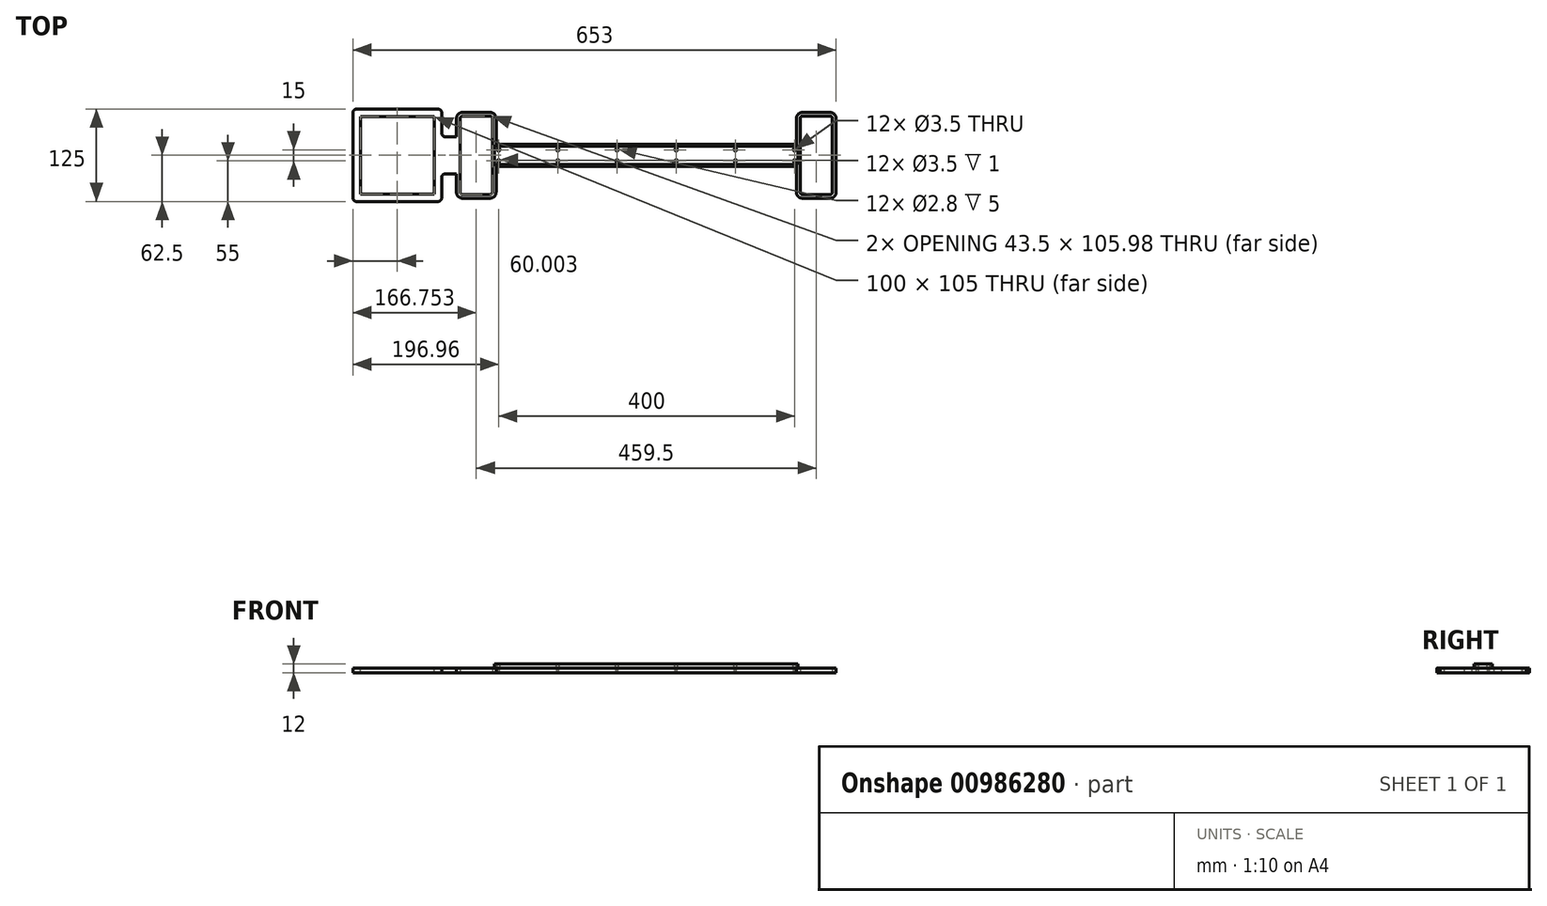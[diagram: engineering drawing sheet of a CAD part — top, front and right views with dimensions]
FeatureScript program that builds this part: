
annotation { "Feature Type Name" : "Feature", "Feature Type Description" : "" }
export const myFeature = defineFeature(function(context is Context, id is Id, definition is map)
    precondition{}
    {
        {
            var Q0;
            Q0=qCreatedBy(makeId("Top.planeOp"),FACE);
            var sketch = newSketch(context, id + "F0", { "sketchPlane" : qUnion([Q0])});
            skLineSegment(sketch, "E0.0", {"start": v(-21.69, 50) * mm, "end": v(-21.69, -50) * mm});
            skLineSegment(sketch, "E1.0", {"start": v(-18.69, 53) * mm, "end": v(18.81, 53) * mm});
            skPoint(sketch, "E2.0", {"position": v(-20.8, 52.11) * mm});
            skPoint(sketch, "E3.0", {"position": v(20.93, 52.11) * mm});
            skLineSegment(sketch, "E4.0", {"start": v(21.81, 50) * mm, "end": v(21.81, -50) * mm});
            skCircle(sketch, "E5.0", {"center": v(12.31, 33) * mm, "radius": 1.75 * mm});
            skCircle(sketch, "E6.0", {"center": v(-12.69, 33) * mm, "radius": 1.75 * mm});
            skArc(sketch, "E7.0", {"start": v(-18.69, 53) * mm, "mid": v(-20.8, 52.11) * mm, "end": v(-21.69, 50) * mm});
            skArc(sketch, "E8.0", {"start": v(21.81, 50) * mm, "mid": v(20.93, 52.11) * mm, "end": v(18.81, 53) * mm});
            skCircle(sketch, "E9.0", {"center": v(12.31, -33) * mm, "radius": 1.75 * mm});
            skCircle(sketch, "E10.0", {"center": v(-12.69, -33) * mm, "radius": 1.75 * mm});
            skPoint(sketch, "E11.0", {"position": v(-20.8, -52.11) * mm});
            skArc(sketch, "E12.0", {"start": v(-21.69, -50) * mm, "mid": v(-20.8, -52.11) * mm, "end": v(-18.69, -53) * mm});
            skLineSegment(sketch, "E13.0", {"start": v(18.81, -53) * mm, "end": v(-18.69, -53) * mm});
            skPoint(sketch, "E14.0", {"position": v(20.93, -52.11) * mm});
            skArc(sketch, "E15.0", {"start": v(18.81, -53) * mm, "mid": v(20.93, -52.11) * mm, "end": v(21.81, -50) * mm});
            skSolve(sketch);
        }
        {
            var Q0;
            Q0=makeQuery(id+"F0.imprint","IMPRINT",FACE,{"disambiguationData":[TD([[makeQuery(id+"F0.imprint","IMPRINT",EDGE,{"derivedFrom":sQuery(id+"F0.wireOp",EDGE,"E0.0")}),1.0]])]});
            extrude(context, id + "F1", {"entities" : qUnion([Q0]), "depth" : 3 * mm, "offsetDistance" : 25 * mm});
        }
        {
            var Q0;
            Q0=qCreatedBy(makeId("Top.planeOp"),FACE);
            var sketch = newSketch(context, id + "F2", { "sketchPlane" : qUnion([Q0])});
            skArc(sketch, "E16.0", {"start": v(-18.69, 58) * mm, "mid": v(-24.34, 55.65) * mm, "end": v(-26.69, 50) * mm});
            skLineSegment(sketch, "E16.1", {"start": v(-18.69, 58) * mm, "end": v(18.81, 58) * mm});
            skLineSegment(sketch, "E16.2", {"start": v(-26.69, 50) * mm, "end": v(-26.69, 30) * mm});
            skArc(sketch, "E16.3", {"start": v(26.81, 50) * mm, "mid": v(24.47, 55.65) * mm, "end": v(18.81, 58) * mm});
            skArc(sketch, "E16.4", {"start": v(-26.69, -50) * mm, "mid": v(-24.34, -55.65) * mm, "end": v(-18.69, -58) * mm});
            skLineSegment(sketch, "E16.5", {"start": v(18.81, -58) * mm, "end": v(-18.69, -58) * mm});
            skArc(sketch, "E16.6", {"start": v(18.81, -58) * mm, "mid": v(24.47, -55.65) * mm, "end": v(26.81, -50) * mm});
            skLineSegment(sketch, "E16.7", {"start": v(26.81, 50) * mm, "end": v(26.81, -50) * mm});
            skLineSegment(sketch, "E17", {"start": v(-21.69, 0) * mm, "end": v(-227.69, 0) * mm});
            skLineSegment(sketch, "E18.0", {"start": v(-26.69, -30) * mm, "end": v(-229.69, -30) * mm});
            skLineSegment(sketch, "E19.0", {"start": v(-26.69, 30) * mm, "end": v(-229.69, 30) * mm});
            skLineSegment(sketch, "E20", {"start": v(-229.69, 30) * mm, "end": v(-229.69, -30) * mm});
            skLineSegment(sketch, "E21.trimOffspring", {"start": v(-26.69, -30) * mm, "end": v(-26.69, -50) * mm});
            skLineSegment(sketch, "E22.0", {"start": v(-21.69, 50) * mm, "end": v(-21.69, -50) * mm});
            skLineSegment(sketch, "E23.0", {"start": v(-18.69, 53) * mm, "end": v(18.81, 53) * mm});
            skLineSegment(sketch, "E24.0", {"start": v(21.81, 50) * mm, "end": v(21.81, -50) * mm});
            skLineSegment(sketch, "E25.0", {"start": v(18.81, -53) * mm, "end": v(-18.69, -53) * mm});
            skArc(sketch, "E26.0", {"start": v(-21.69, -50) * mm, "mid": v(-20.8, -52.11) * mm, "end": v(-18.69, -53) * mm});
            skArc(sketch, "E27.0", {"start": v(18.81, -53) * mm, "mid": v(20.93, -52.11) * mm, "end": v(21.81, -50) * mm});
            skArc(sketch, "E28.0", {"start": v(21.81, 50) * mm, "mid": v(20.93, 52.11) * mm, "end": v(18.81, 53) * mm});
            skArc(sketch, "E29.0", {"start": v(-18.69, 53) * mm, "mid": v(-20.8, 52.11) * mm, "end": v(-21.69, 50) * mm});
            skSolve(sketch);
        }
        {
            var Q0;
            Q0=makeQuery(id+"F2.imprint","IMPRINT",FACE,{"disambiguationData":[TD([[makeQuery(id+"F2.imprint","IMPRINT",EDGE,{"derivedFrom":sQuery(id+"F2.wireOp",EDGE,"E16.0")}),1.0]])]});
            extrude(context, id + "F3", {"entities" : qUnion([Q0]), "operationType" : NewBodyOperationType.ADD, "depth" : 6 * mm, "offsetDistance" : 25 * mm});
        }
        {
            var Q0;
            Q0=makeQuery(id+"F3.opExtrude","SWEPT_FACE",FACE,{"disambiguationData":[OSD([sQuery(id+"F2.wireOp",EDGE,"E20")])]});
            cPlane(context, id + "F4", {"entities" : qUnion([Q0]), "cplaneType" : CPlaneType.OFFSET, "offset" : 0 * mm, "width" : 150 * mm, "height" : 150 * mm});
        }
        {
            var Q0;
            Q0=makeQuery(id+"F1.opExtrude","SWEPT_BODY",BODY,{"disambiguationData":[OSD([sQuery(id+"F0.wireOp",EDGE,"E0.0"),sQuery(id+"F0.wireOp",EDGE,"E1.0"),sQuery(id+"F0.wireOp",EDGE,"E4.0"),sQuery(id+"F0.wireOp",EDGE,"E5.0"),sQuery(id+"F0.wireOp",EDGE,"E6.0"),sQuery(id+"F0.wireOp",EDGE,"E7.0"),sQuery(id+"F0.wireOp",EDGE,"E8.0"),sQuery(id+"F0.wireOp",EDGE,"E9.0"),sQuery(id+"F0.wireOp",EDGE,"E10.0"),sQuery(id+"F0.wireOp",EDGE,"E12.0"),sQuery(id+"F0.wireOp",EDGE,"E13.0"),sQuery(id+"F0.wireOp",EDGE,"E15.0")])]});
            var Q1;
            Q1=qCreatedBy(id+"F4.planeOp",FACE);
            mirror(context, id + "F5", {"operationType" : NewBodyOperationType.ADD, "entities" : qUnion([Q0]), "mirrorPlane" : qUnion([Q1])});
        }
        {
            var Q0;
            {var subQ0=makeQuery(id+"F3.opExtrude","CAP_FACE",FACE,{"disambiguationData":[OSD([sQuery(id+"F2.wireOp",EDGE,"E16.0"),sQuery(id+"F2.wireOp",EDGE,"E16.1"),sQuery(id+"F2.wireOp",EDGE,"E16.2"),sQuery(id+"F2.wireOp",EDGE,"E16.3"),sQuery(id+"F2.wireOp",EDGE,"E16.4"),sQuery(id+"F2.wireOp",EDGE,"E16.5"),sQuery(id+"F2.wireOp",EDGE,"E16.6"),sQuery(id+"F2.wireOp",EDGE,"E16.7"),sQuery(id+"F2.wireOp",EDGE,"E18.0"),sQuery(id+"F2.wireOp",EDGE,"E19.0"),sQuery(id+"F2.wireOp",EDGE,"E20"),sQuery(id+"F2.wireOp",EDGE,"E21.trimOffspring"),sQuery(id+"F2.wireOp",EDGE,"E22.0"),sQuery(id+"F2.wireOp",EDGE,"E23.0"),sQuery(id+"F2.wireOp",EDGE,"E24.0"),sQuery(id+"F2.wireOp",EDGE,"E25.0"),sQuery(id+"F2.wireOp",EDGE,"E26.0"),sQuery(id+"F2.wireOp",EDGE,"E27.0"),sQuery(id+"F2.wireOp",EDGE,"E28.0"),sQuery(id+"F2.wireOp",EDGE,"E29.0")])],"isStart":false});Q0=makeQuery(id+"F5.boolean.opBoolean","MERGE",FACE,{"derivedFrom":[subQ0,makeQuery(id+"F5.opPattern","COPY",FACE,{"derivedFrom":subQ0,"instanceName":"1"})]});}
            var sketch = newSketch(context, id + "F6", { "sketchPlane" : qUnion([Q0])});
            skLineSegment(sketch, "E30", {"start": v(-229.69, 30) * mm, "end": v(-169.69, 30) * mm});
            skLineSegment(sketch, "E31", {"start": v(-169.69, 30) * mm, "end": v(-169.69, 58) * mm});
            skLineSegment(sketch, "E32", {"start": v(-169.69, 58) * mm, "end": v(-289.69, 58) * mm});
            skLineSegment(sketch, "E33", {"start": v(-289.69, 58) * mm, "end": v(-289.69, 30) * mm});
            skLineSegment(sketch, "E34", {"start": v(-289.69, 30) * mm, "end": v(-229.69, 30) * mm});
            skSolve(sketch);
        }
        {
            var Q0;
            Q0=makeQuery(id+"F6.imprint","IMPRINT",FACE,{"disambiguationData":[TD([[makeQuery(id+"F6.imprint","IMPRINT",EDGE,{"derivedFrom":sQuery(id+"F6.wireOp",EDGE,"E30")}),-1.0]])]});
            var Q1;
            {var subQ0=makeQuery(id+"F3.boolean.opBoolean","MERGE",FACE,{"derivedFrom":[makeQuery(id+"F1.opExtrude","CAP_FACE",FACE,{"disambiguationData":[OSD([sQuery(id+"F0.wireOp",EDGE,"E0.0"),sQuery(id+"F0.wireOp",EDGE,"E1.0"),sQuery(id+"F0.wireOp",EDGE,"E4.0"),sQuery(id+"F0.wireOp",EDGE,"E5.0"),sQuery(id+"F0.wireOp",EDGE,"E6.0"),sQuery(id+"F0.wireOp",EDGE,"E7.0"),sQuery(id+"F0.wireOp",EDGE,"E8.0"),sQuery(id+"F0.wireOp",EDGE,"E9.0"),sQuery(id+"F0.wireOp",EDGE,"E10.0"),sQuery(id+"F0.wireOp",EDGE,"E12.0"),sQuery(id+"F0.wireOp",EDGE,"E13.0"),sQuery(id+"F0.wireOp",EDGE,"E15.0")])],"isStart":true}),makeQuery(id+"F3.opExtrude","CAP_FACE",FACE,{"disambiguationData":[OSD([sQuery(id+"F2.wireOp",EDGE,"E16.0"),sQuery(id+"F2.wireOp",EDGE,"E16.1"),sQuery(id+"F2.wireOp",EDGE,"E16.2"),sQuery(id+"F2.wireOp",EDGE,"E16.3"),sQuery(id+"F2.wireOp",EDGE,"E16.4"),sQuery(id+"F2.wireOp",EDGE,"E16.5"),sQuery(id+"F2.wireOp",EDGE,"E16.6"),sQuery(id+"F2.wireOp",EDGE,"E16.7"),sQuery(id+"F2.wireOp",EDGE,"E18.0"),sQuery(id+"F2.wireOp",EDGE,"E19.0"),sQuery(id+"F2.wireOp",EDGE,"E20"),sQuery(id+"F2.wireOp",EDGE,"E21.trimOffspring"),sQuery(id+"F2.wireOp",EDGE,"E22.0"),sQuery(id+"F2.wireOp",EDGE,"E23.0"),sQuery(id+"F2.wireOp",EDGE,"E24.0"),sQuery(id+"F2.wireOp",EDGE,"E25.0"),sQuery(id+"F2.wireOp",EDGE,"E26.0"),sQuery(id+"F2.wireOp",EDGE,"E27.0"),sQuery(id+"F2.wireOp",EDGE,"E28.0"),sQuery(id+"F2.wireOp",EDGE,"E29.0")])],"isStart":true})]});Q1=makeQuery(id+"F5.boolean.opBoolean","MERGE",FACE,{"derivedFrom":[subQ0,makeQuery(id+"F5.opPattern","COPY",FACE,{"derivedFrom":subQ0,"instanceName":"1"})]});}
            extrude(context, id + "F7", {"entities" : qUnion([Q0]), "operationType" : NewBodyOperationType.ADD, "endBound" : BoundingType.UP_TO_SURFACE, "oppositeDirection" : true, "depth" : 25 * mm, "endBoundEntityFace" : qUnion([Q1]), "offsetDistance" : 25 * mm});
        }
        {
            var Q0;
            Q0=makeQuery(id+"F7.opExtrude","SWEPT_EDGE",EDGE,{"disambiguationData":[OSD([sQuery(id+"F6.wireOp",EDGE,"E31"),sQuery(id+"F6.wireOp",EDGE,"E32")])]});
            var Q1;
            Q1=makeQuery(id+"F7.opExtrude","SWEPT_EDGE",EDGE,{"disambiguationData":[OSD([sQuery(id+"F2.wireOp",EDGE,"E19.0"),sQuery(id+"F6.wireOp",EDGE,"E30"),sQuery(id+"F6.wireOp",EDGE,"E31")])]});
            var Q2;
            Q2=makeQuery(id+"F7.opExtrude","SWEPT_EDGE",EDGE,{"disambiguationData":[OSD([sQuery(id+"F6.wireOp",EDGE,"E32"),sQuery(id+"F6.wireOp",EDGE,"E33")])]});
            var Q3;
            Q3=makeQuery(id+"F7.opExtrude","SWEPT_EDGE",EDGE,{"disambiguationData":[OSD([sQuery(id+"F2.wireOp",EDGE,"E19.0"),sQuery(id+"F6.wireOp",EDGE,"E33"),sQuery(id+"F6.wireOp",EDGE,"E34")])]});
            fillet(context, id + "F8", {"entities" : qUnion([Q0, Q1, Q2, Q3]), "radius" : 10 * mm, "tangentPropagation" : true, "allowEdgeOverflow" : false});
        }
        {
            var Q0;
            {var subQ0=makeQuery(id+"F3.opExtrude","CAP_FACE",FACE,{"disambiguationData":[OSD([sQuery(id+"F2.wireOp",EDGE,"E16.0"),sQuery(id+"F2.wireOp",EDGE,"E16.1"),sQuery(id+"F2.wireOp",EDGE,"E16.2"),sQuery(id+"F2.wireOp",EDGE,"E16.3"),sQuery(id+"F2.wireOp",EDGE,"E16.4"),sQuery(id+"F2.wireOp",EDGE,"E16.5"),sQuery(id+"F2.wireOp",EDGE,"E16.6"),sQuery(id+"F2.wireOp",EDGE,"E16.7"),sQuery(id+"F2.wireOp",EDGE,"E18.0"),sQuery(id+"F2.wireOp",EDGE,"E19.0"),sQuery(id+"F2.wireOp",EDGE,"E20"),sQuery(id+"F2.wireOp",EDGE,"E21.trimOffspring"),sQuery(id+"F2.wireOp",EDGE,"E22.0"),sQuery(id+"F2.wireOp",EDGE,"E23.0"),sQuery(id+"F2.wireOp",EDGE,"E24.0"),sQuery(id+"F2.wireOp",EDGE,"E25.0"),sQuery(id+"F2.wireOp",EDGE,"E26.0"),sQuery(id+"F2.wireOp",EDGE,"E27.0"),sQuery(id+"F2.wireOp",EDGE,"E28.0"),sQuery(id+"F2.wireOp",EDGE,"E29.0")])],"isStart":false});Q0=makeQuery(id+"F7.boolean.opBoolean","MERGE",FACE,{"derivedFrom":[makeQuery(id+"F5.boolean.opBoolean","MERGE",FACE,{"derivedFrom":[subQ0,makeQuery(id+"F5.opPattern","COPY",FACE,{"derivedFrom":subQ0,"instanceName":"1"})]}),makeQuery(id+"F7.opExtrude","CAP_FACE",FACE,{"disambiguationData":[OSD([sQuery(id+"F6.wireOp",EDGE,"E30"),sQuery(id+"F6.wireOp",EDGE,"E31"),sQuery(id+"F6.wireOp",EDGE,"E32"),sQuery(id+"F6.wireOp",EDGE,"E33"),sQuery(id+"F6.wireOp",EDGE,"E34")])],"isStart":true})]});}
            var sketch = newSketch(context, id + "F9", { "sketchPlane" : qUnion([Q0])});
            skLineSegment(sketch, "E35", {"start": v(-437.69, 0) * mm, "end": v(-13.9, 0) * mm, "construction": true});
            skLineSegment(sketch, "E36.bottom", {"start": v(-274.69, 23) * mm, "end": v(-184.69, 23) * mm});
            skLineSegment(sketch, "E36.top", {"start": v(-274.69, 48) * mm, "end": v(-184.69, 48) * mm});
            skLineSegment(sketch, "E36.left", {"start": v(-279.69, 28) * mm, "end": v(-279.69, 43) * mm});
            skLineSegment(sketch, "E36.right", {"start": v(-179.69, 28) * mm, "end": v(-179.69, 43) * mm});
            skPoint(sketch, "E36.middle", {"position": v(-229.69, 35.5) * mm});
            skPoint(sketch, "E37.visualSharp", {"position": v(-279.69, 48) * mm});
            skArc(sketch, "E37.filletArc", {"start": v(-274.69, 48) * mm, "mid": v(-278.22, 46.53) * mm, "end": v(-279.69, 43) * mm});
            skPoint(sketch, "E38.visualSharp", {"position": v(-179.69, 48) * mm});
            skArc(sketch, "E38.filletArc", {"start": v(-179.69, 43) * mm, "mid": v(-181.15, 46.53) * mm, "end": v(-184.69, 48) * mm});
            skPoint(sketch, "E39.visualSharp", {"position": v(-179.69, 23) * mm});
            skArc(sketch, "E39.filletArc", {"start": v(-184.69, 23) * mm, "mid": v(-181.15, 24.45) * mm, "end": v(-179.69, 28) * mm});
            skPoint(sketch, "E40.visualSharp", {"position": v(-279.69, 23) * mm});
            skArc(sketch, "E40.filletArc", {"start": v(-279.69, 28) * mm, "mid": v(-278.22, 24.45) * mm, "end": v(-274.69, 23) * mm});
            skSolve(sketch);
        }
        {
            var Q0;
            Q0=makeQuery(id+"F9.imprint","IMPRINT",FACE,{"disambiguationData":[TD([[makeQuery(id+"F9.imprint","IMPRINT",EDGE,{"derivedFrom":sQuery(id+"F9.wireOp",EDGE,"E36.bottom")}),1.0]])]});
            extrude(context, id + "F10", {"entities" : qUnion([Q0]), "operationType" : NewBodyOperationType.REMOVE, "oppositeDirection" : true, "depth" : 25 * mm, "offsetDistance" : 25 * mm});
        }
        {
            var Q0;
            Q0=makeQuery(id+"F5.opPattern","COPY",EDGE,{"derivedFrom":makeQuery(id+"F3.opExtrude","SWEPT_EDGE",EDGE,{"disambiguationData":[OSD([sQuery(id+"F2.wireOp",EDGE,"E16.2"),sQuery(id+"F2.wireOp",EDGE,"E19.0")])]}),"instanceName":"1"});
            var Q1;
            Q1=makeQuery(id+"F5.opPattern","COPY",EDGE,{"derivedFrom":makeQuery(id+"F3.opExtrude","SWEPT_EDGE",EDGE,{"disambiguationData":[OSD([sQuery(id+"F2.wireOp",EDGE,"E18.0"),sQuery(id+"F2.wireOp",EDGE,"E21.trimOffspring")])]}),"instanceName":"1"});
            var Q2;
            Q2=makeQuery(id+"F3.opExtrude","SWEPT_EDGE",EDGE,{"disambiguationData":[OSD([sQuery(id+"F2.wireOp",EDGE,"E18.0"),sQuery(id+"F2.wireOp",EDGE,"E21.trimOffspring")])]});
            var Q3;
            Q3=makeQuery(id+"F3.opExtrude","SWEPT_EDGE",EDGE,{"disambiguationData":[OSD([sQuery(id+"F2.wireOp",EDGE,"E16.2"),sQuery(id+"F2.wireOp",EDGE,"E19.0")])]});
            fillet(context, id + "F11", {"entities" : qUnion([Q0, Q1, Q2, Q3]), "radius" : 5 * mm, "tangentPropagation" : true, "allowEdgeOverflow" : false});
        }
        {
            var Q0;
            {var subQ0=makeQuery(id+"F3.opExtrude","CAP_FACE",FACE,{"disambiguationData":[OSD([sQuery(id+"F2.wireOp",EDGE,"E16.0"),sQuery(id+"F2.wireOp",EDGE,"E16.1"),sQuery(id+"F2.wireOp",EDGE,"E16.2"),sQuery(id+"F2.wireOp",EDGE,"E16.3"),sQuery(id+"F2.wireOp",EDGE,"E16.4"),sQuery(id+"F2.wireOp",EDGE,"E16.5"),sQuery(id+"F2.wireOp",EDGE,"E16.6"),sQuery(id+"F2.wireOp",EDGE,"E16.7"),sQuery(id+"F2.wireOp",EDGE,"E18.0"),sQuery(id+"F2.wireOp",EDGE,"E19.0"),sQuery(id+"F2.wireOp",EDGE,"E20"),sQuery(id+"F2.wireOp",EDGE,"E21.trimOffspring"),sQuery(id+"F2.wireOp",EDGE,"E22.0"),sQuery(id+"F2.wireOp",EDGE,"E23.0"),sQuery(id+"F2.wireOp",EDGE,"E24.0"),sQuery(id+"F2.wireOp",EDGE,"E25.0"),sQuery(id+"F2.wireOp",EDGE,"E26.0"),sQuery(id+"F2.wireOp",EDGE,"E27.0"),sQuery(id+"F2.wireOp",EDGE,"E28.0"),sQuery(id+"F2.wireOp",EDGE,"E29.0")])],"isStart":false});Q0=makeQuery(id+"F7.boolean.opBoolean","MERGE",FACE,{"derivedFrom":[makeQuery(id+"F5.boolean.opBoolean","MERGE",FACE,{"derivedFrom":[subQ0,makeQuery(id+"F5.opPattern","COPY",FACE,{"derivedFrom":subQ0,"instanceName":"1"})]}),makeQuery(id+"F7.opExtrude","CAP_FACE",FACE,{"disambiguationData":[OSD([sQuery(id+"F6.wireOp",EDGE,"E30"),sQuery(id+"F6.wireOp",EDGE,"E31"),sQuery(id+"F6.wireOp",EDGE,"E32"),sQuery(id+"F6.wireOp",EDGE,"E33"),sQuery(id+"F6.wireOp",EDGE,"E34")])],"isStart":true})]});}
            var sketch = newSketch(context, id + "F12", { "sketchPlane" : qUnion([Q0])});
            skLineSegment(sketch, "E41", {"start": v(-229.69, 0) * mm, "end": v(-229.69, 17.75) * mm, "construction": true});
            skPoint(sketch, "E41.startSnap0", {"position": v(-229.69, -30) * mm});
            skLineSegment(sketch, "E42.bottom", {"start": v(-434.69, -12.5) * mm, "end": v(-24.69, -12.5) * mm});
            skLineSegment(sketch, "E42.top", {"start": v(-434.69, 12.5) * mm, "end": v(-24.69, 12.5) * mm});
            skLineSegment(sketch, "E42.left", {"start": v(-434.69, -12.5) * mm, "end": v(-434.69, 12.5) * mm});
            skLineSegment(sketch, "E42.right", {"start": v(-24.69, -12.5) * mm, "end": v(-24.69, 12.5) * mm});
            skPoint(sketch, "E42.middle", {"position": v(-229.69, 0) * mm});
            skSolve(sketch);
        }
        {
            var Q0;
            Q0=makeQuery(id+"F12.imprint","IMPRINT",FACE,{"disambiguationData":[TD([[makeQuery(id+"F12.imprint","IMPRINT",EDGE,{"derivedFrom":sQuery(id+"F12.wireOp",EDGE,"E42.bottom")}),1.0]])]});
            extrude(context, id + "F13", {"entities" : qUnion([Q0]), "depth" : 6 * mm, "offsetDistance" : 25 * mm});
        }
        {
            var Q0;
            Q0=makeQuery(id+"F13.opExtrude","CAP_FACE",FACE,{"disambiguationData":[OSD([sQuery(id+"F12.wireOp",EDGE,"E42.bottom"),sQuery(id+"F12.wireOp",EDGE,"E42.top"),sQuery(id+"F12.wireOp",EDGE,"E42.left"),sQuery(id+"F12.wireOp",EDGE,"E42.right")])],"isStart":false});
            var sketch = newSketch(context, id + "F14", { "sketchPlane" : qUnion([Q0])});
            skLineSegment(sketch, "E43.bottom", {"start": v(-429.23, -7.5) * mm, "end": v(-29.23, -7.5) * mm, "construction": true});
            skLineSegment(sketch, "E43.top", {"start": v(-429.23, 7.5) * mm, "end": v(-29.23, 7.5) * mm, "construction": true});
            skLineSegment(sketch, "E43.left", {"start": v(-429.23, -7.5) * mm, "end": v(-429.23, 7.5) * mm, "construction": true});
            skLineSegment(sketch, "E43.right", {"start": v(-29.23, -7.5) * mm, "end": v(-29.23, 7.5) * mm, "construction": true});
            skPoint(sketch, "E43.middle", {"position": v(-229.23, 0) * mm});
            skCircle(sketch, "E44", {"center": v(-429.23, 7.5) * mm, "radius": 1.75 * mm});
            skCircle(sketch, "E45", {"center": v(-429.23, -7.5) * mm, "radius": 1.75 * mm});
            skCircle(sketch, "E46.1.0.0", {"center": v(-349.23, 7.5) * mm, "radius": 1.75 * mm});
            skCircle(sketch, "E46.2.0.0", {"center": v(-269.23, 7.5) * mm, "radius": 1.75 * mm});
            skCircle(sketch, "E46.3.0.0", {"center": v(-189.23, 7.5) * mm, "radius": 1.75 * mm});
            skCircle(sketch, "E46.4.0.0", {"center": v(-109.23, 7.5) * mm, "radius": 1.75 * mm});
            skLineSegment(sketch, "E46.direction1", {"start": v(-429.23, 7.5) * mm, "end": v(-349.23, 7.5) * mm, "construction": true});
            skCircle(sketch, "E47.1.0.0", {"center": v(-349.23, -7.5) * mm, "radius": 1.75 * mm});
            skCircle(sketch, "E47.2.0.0", {"center": v(-269.23, -7.5) * mm, "radius": 1.75 * mm});
            skCircle(sketch, "E47.3.0.0", {"center": v(-189.23, -7.5) * mm, "radius": 1.75 * mm});
            skCircle(sketch, "E47.4.0.0", {"center": v(-109.23, -7.5) * mm, "radius": 1.75 * mm});
            skLineSegment(sketch, "E47.direction1", {"start": v(-429.23, -7.5) * mm, "end": v(-349.23, -7.5) * mm, "construction": true});
            skCircle(sketch, "E48.0.5.0", {"center": v(-29.23, -7.5) * mm, "radius": 1.75 * mm});
            skCircle(sketch, "E49.0.5.0", {"center": v(-29.23, 7.5) * mm, "radius": 1.75 * mm});
            skSolve(sketch);
        }
        {
            var Q0;
            Q0=makeQuery(id+"F14.imprint","IMPRINT",FACE,{"disambiguationData":[TD([[makeQuery(id+"F14.imprint","IMPRINT",EDGE,{"derivedFrom":sQuery(id+"F14.wireOp",EDGE,"E44")}),1.0]])]});
            var Q1;
            Q1=makeQuery(id+"F14.imprint","IMPRINT",FACE,{"disambiguationData":[TD([[makeQuery(id+"F14.imprint","IMPRINT",EDGE,{"derivedFrom":sQuery(id+"F14.wireOp",EDGE,"E45")}),1.0]])]});
            var Q2;
            Q2=makeQuery(id+"F14.imprint","IMPRINT",FACE,{"disambiguationData":[TD([[makeQuery(id+"F14.imprint","IMPRINT",EDGE,{"derivedFrom":sQuery(id+"F14.wireOp",EDGE,"E47.1.0.0")}),1.0]])]});
            var Q3;
            Q3=makeQuery(id+"F14.imprint","IMPRINT",FACE,{"disambiguationData":[TD([[makeQuery(id+"F14.imprint","IMPRINT",EDGE,{"derivedFrom":sQuery(id+"F14.wireOp",EDGE,"E46.1.0.0")}),1.0]])]});
            var Q4;
            Q4=makeQuery(id+"F14.imprint","IMPRINT",FACE,{"disambiguationData":[TD([[makeQuery(id+"F14.imprint","IMPRINT",EDGE,{"derivedFrom":sQuery(id+"F14.wireOp",EDGE,"E46.2.0.0")}),1.0]])]});
            var Q5;
            Q5=makeQuery(id+"F14.imprint","IMPRINT",FACE,{"disambiguationData":[TD([[makeQuery(id+"F14.imprint","IMPRINT",EDGE,{"derivedFrom":sQuery(id+"F14.wireOp",EDGE,"E47.2.0.0")}),1.0]])]});
            var Q6;
            Q6=makeQuery(id+"F14.imprint","IMPRINT",FACE,{"disambiguationData":[TD([[makeQuery(id+"F14.imprint","IMPRINT",EDGE,{"derivedFrom":sQuery(id+"F14.wireOp",EDGE,"E47.3.0.0")}),1.0]])]});
            var Q7;
            Q7=makeQuery(id+"F14.imprint","IMPRINT",FACE,{"disambiguationData":[TD([[makeQuery(id+"F14.imprint","IMPRINT",EDGE,{"derivedFrom":sQuery(id+"F14.wireOp",EDGE,"E46.3.0.0")}),1.0]])]});
            var Q8;
            Q8=makeQuery(id+"F14.imprint","IMPRINT",FACE,{"disambiguationData":[TD([[makeQuery(id+"F14.imprint","IMPRINT",EDGE,{"derivedFrom":sQuery(id+"F14.wireOp",EDGE,"E47.4.0.0")}),1.0]])]});
            var Q9;
            Q9=makeQuery(id+"F14.imprint","IMPRINT",FACE,{"disambiguationData":[TD([[makeQuery(id+"F14.imprint","IMPRINT",EDGE,{"derivedFrom":sQuery(id+"F14.wireOp",EDGE,"E46.4.0.0")}),1.0]])]});
            var Q10;
            Q10=makeQuery(id+"F14.imprint","IMPRINT",FACE,{"disambiguationData":[TD([[makeQuery(id+"F14.imprint","IMPRINT",EDGE,{"derivedFrom":sQuery(id+"F14.wireOp",EDGE,"E48.0.5.0")}),1.0]])]});
            var Q11;
            Q11=makeQuery(id+"F14.imprint","IMPRINT",FACE,{"disambiguationData":[TD([[makeQuery(id+"F14.imprint","IMPRINT",EDGE,{"derivedFrom":sQuery(id+"F14.wireOp",EDGE,"E49.0.5.0")}),1.0]])]});
            extrude(context, id + "F15", {"entities" : qUnion([Q0, Q1, Q2, Q3, Q4, Q5, Q6, Q7, Q8, Q9, Q10, Q11]), "operationType" : NewBodyOperationType.REMOVE, "oppositeDirection" : true, "depth" : 7 * mm, "offsetDistance" : 25 * mm});
        }
        {
            var Q0;
            {var subQ0=makeQuery(id+"F3.opExtrude","CAP_FACE",FACE,{"disambiguationData":[OSD([sQuery(id+"F2.wireOp",EDGE,"E16.0"),sQuery(id+"F2.wireOp",EDGE,"E16.1"),sQuery(id+"F2.wireOp",EDGE,"E16.2"),sQuery(id+"F2.wireOp",EDGE,"E16.3"),sQuery(id+"F2.wireOp",EDGE,"E16.4"),sQuery(id+"F2.wireOp",EDGE,"E16.5"),sQuery(id+"F2.wireOp",EDGE,"E16.6"),sQuery(id+"F2.wireOp",EDGE,"E16.7"),sQuery(id+"F2.wireOp",EDGE,"E18.0"),sQuery(id+"F2.wireOp",EDGE,"E19.0"),sQuery(id+"F2.wireOp",EDGE,"E20"),sQuery(id+"F2.wireOp",EDGE,"E21.trimOffspring"),sQuery(id+"F2.wireOp",EDGE,"E22.0"),sQuery(id+"F2.wireOp",EDGE,"E23.0"),sQuery(id+"F2.wireOp",EDGE,"E24.0"),sQuery(id+"F2.wireOp",EDGE,"E25.0"),sQuery(id+"F2.wireOp",EDGE,"E26.0"),sQuery(id+"F2.wireOp",EDGE,"E27.0"),sQuery(id+"F2.wireOp",EDGE,"E28.0"),sQuery(id+"F2.wireOp",EDGE,"E29.0")])],"isStart":false});Q0=makeQuery(id+"F7.boolean.opBoolean","MERGE",FACE,{"derivedFrom":[makeQuery(id+"F5.boolean.opBoolean","MERGE",FACE,{"derivedFrom":[subQ0,makeQuery(id+"F5.opPattern","COPY",FACE,{"derivedFrom":subQ0,"instanceName":"1"})]}),makeQuery(id+"F7.opExtrude","CAP_FACE",FACE,{"disambiguationData":[OSD([sQuery(id+"F6.wireOp",EDGE,"E30"),sQuery(id+"F6.wireOp",EDGE,"E31"),sQuery(id+"F6.wireOp",EDGE,"E32"),sQuery(id+"F6.wireOp",EDGE,"E33"),sQuery(id+"F6.wireOp",EDGE,"E34")])],"isStart":true})]});}
            var sketch = newSketch(context, id + "F16", { "sketchPlane" : qUnion([Q0])});
            skCircle(sketch, "E50", {"center": v(-429.23, 7.5) * mm, "radius": 1.4 * mm});
            skCircle(sketch, "E51.1.0.0", {"center": v(-349.23, 7.5) * mm, "radius": 1.4 * mm});
            skCircle(sketch, "E51.2.0.0", {"center": v(-269.23, 7.5) * mm, "radius": 1.4 * mm});
            skLineSegment(sketch, "E51.direction1", {"start": v(-429.23, 7.5) * mm, "end": v(-349.23, 7.5) * mm, "construction": true});
            skCircle(sketch, "E52.0.3.0", {"center": v(-189.23, 7.5) * mm, "radius": 1.4 * mm});
            skCircle(sketch, "E52.0.4.0", {"center": v(-109.23, 7.5) * mm, "radius": 1.4 * mm});
            skCircle(sketch, "E52.0.5.0", {"center": v(-29.23, 7.5) * mm, "radius": 1.4 * mm});
            skCircle(sketch, "E53", {"center": v(-429.23, -7.5) * mm, "radius": 1.4 * mm});
            skCircle(sketch, "E54.1.0.0", {"center": v(-349.23, -7.5) * mm, "radius": 1.4 * mm});
            skCircle(sketch, "E54.2.0.0", {"center": v(-269.23, -7.5) * mm, "radius": 1.4 * mm});
            skLineSegment(sketch, "E54.direction1", {"start": v(-429.23, -7.5) * mm, "end": v(-349.23, -7.5) * mm, "construction": true});
            skCircle(sketch, "E55.0.3.0", {"center": v(-189.23, -7.5) * mm, "radius": 1.4 * mm});
            skCircle(sketch, "E55.0.4.0", {"center": v(-109.23, -7.5) * mm, "radius": 1.4 * mm});
            skCircle(sketch, "E55.0.5.0", {"center": v(-29.23, -7.5) * mm, "radius": 1.4 * mm});
            skSolve(sketch);
        }
        {
            var Q0;
            Q0 = qSketchRegion(id + "F16", true);
            extrude(context, id + "F17", {"entities" : qUnion([Q0]), "operationType" : NewBodyOperationType.REMOVE, "oppositeDirection" : true, "depth" : 25 * mm, "offsetDistance" : 25 * mm});
        }
        {
            var Q0;
            Q0=makeQuery(id+"F5.opPattern","COPY",FACE,{"derivedFrom":makeQuery(id+"F1.opExtrude","CAP_FACE",FACE,{"disambiguationData":[OSD([sQuery(id+"F0.wireOp",EDGE,"E0.0"),sQuery(id+"F0.wireOp",EDGE,"E1.0"),sQuery(id+"F0.wireOp",EDGE,"E4.0"),sQuery(id+"F0.wireOp",EDGE,"E5.0"),sQuery(id+"F0.wireOp",EDGE,"E6.0"),sQuery(id+"F0.wireOp",EDGE,"E7.0"),sQuery(id+"F0.wireOp",EDGE,"E8.0"),sQuery(id+"F0.wireOp",EDGE,"E9.0"),sQuery(id+"F0.wireOp",EDGE,"E10.0"),sQuery(id+"F0.wireOp",EDGE,"E12.0"),sQuery(id+"F0.wireOp",EDGE,"E13.0"),sQuery(id+"F0.wireOp",EDGE,"E15.0")])],"isStart":false}),"instanceName":"1"});
            extrude(context, id + "F18", {"entities" : qUnion([Q0]), "operationType" : NewBodyOperationType.REMOVE, "oppositeDirection" : true, "depth" : 25 * mm, "offsetDistance" : 25 * mm});
        }
        {
            var Q0;
            Q0=makeQuery(id+"F1.opExtrude","CAP_FACE",FACE,{"disambiguationData":[OSD([sQuery(id+"F0.wireOp",EDGE,"E0.0"),sQuery(id+"F0.wireOp",EDGE,"E1.0"),sQuery(id+"F0.wireOp",EDGE,"E4.0"),sQuery(id+"F0.wireOp",EDGE,"E5.0"),sQuery(id+"F0.wireOp",EDGE,"E6.0"),sQuery(id+"F0.wireOp",EDGE,"E7.0"),sQuery(id+"F0.wireOp",EDGE,"E8.0"),sQuery(id+"F0.wireOp",EDGE,"E9.0"),sQuery(id+"F0.wireOp",EDGE,"E10.0"),sQuery(id+"F0.wireOp",EDGE,"E12.0"),sQuery(id+"F0.wireOp",EDGE,"E13.0"),sQuery(id+"F0.wireOp",EDGE,"E15.0")])],"isStart":false});
            extrude(context, id + "F19", {"entities" : qUnion([Q0]), "operationType" : NewBodyOperationType.REMOVE, "oppositeDirection" : true, "depth" : 25 * mm, "offsetDistance" : 25 * mm});
        }
        {
            var Q0;
            {var subQ0=makeQuery(id+"F3.opExtrude","CAP_FACE",FACE,{"disambiguationData":[OSD([sQuery(id+"F2.wireOp",EDGE,"E16.0"),sQuery(id+"F2.wireOp",EDGE,"E16.1"),sQuery(id+"F2.wireOp",EDGE,"E16.2"),sQuery(id+"F2.wireOp",EDGE,"E16.3"),sQuery(id+"F2.wireOp",EDGE,"E16.4"),sQuery(id+"F2.wireOp",EDGE,"E16.5"),sQuery(id+"F2.wireOp",EDGE,"E16.6"),sQuery(id+"F2.wireOp",EDGE,"E16.7"),sQuery(id+"F2.wireOp",EDGE,"E18.0"),sQuery(id+"F2.wireOp",EDGE,"E19.0"),sQuery(id+"F2.wireOp",EDGE,"E20"),sQuery(id+"F2.wireOp",EDGE,"E21.trimOffspring"),sQuery(id+"F2.wireOp",EDGE,"E22.0"),sQuery(id+"F2.wireOp",EDGE,"E23.0"),sQuery(id+"F2.wireOp",EDGE,"E24.0"),sQuery(id+"F2.wireOp",EDGE,"E25.0"),sQuery(id+"F2.wireOp",EDGE,"E26.0"),sQuery(id+"F2.wireOp",EDGE,"E27.0"),sQuery(id+"F2.wireOp",EDGE,"E28.0"),sQuery(id+"F2.wireOp",EDGE,"E29.0")])],"isStart":false});Q0=makeQuery(id+"F7.boolean.opBoolean","MERGE",FACE,{"derivedFrom":[makeQuery(id+"F5.boolean.opBoolean","MERGE",FACE,{"derivedFrom":[subQ0,makeQuery(id+"F5.opPattern","COPY",FACE,{"derivedFrom":subQ0,"instanceName":"1"})]}),makeQuery(id+"F7.opExtrude","CAP_FACE",FACE,{"disambiguationData":[OSD([sQuery(id+"F6.wireOp",EDGE,"E30"),sQuery(id+"F6.wireOp",EDGE,"E31"),sQuery(id+"F6.wireOp",EDGE,"E32"),sQuery(id+"F6.wireOp",EDGE,"E33"),sQuery(id+"F6.wireOp",EDGE,"E34")])],"isStart":true})]});}
            var sketch = newSketch(context, id + "F20", { "sketchPlane" : qUnion([Q0])});
            skLineSegment(sketch, "E56", {"start": v(-432.69, 35) * mm, "end": v(-432.69, -35) * mm});
            skLineSegment(sketch, "E57", {"start": v(-26.69, 35) * mm, "end": v(-26.69, -35) * mm});
            skLineSegment(sketch, "E58", {"start": v(-432.69, 0) * mm, "end": v(-26.69, 0) * mm});
            skLineSegment(sketch, "E59.0", {"start": v(-432.69, -15) * mm, "end": v(-26.69, -15) * mm});
            skLineSegment(sketch, "E60.0", {"start": v(-432.69, 15) * mm, "end": v(-26.69, 15) * mm});
            skLineSegment(sketch, "E61", {"start": v(-432.69, 35) * mm, "end": v(-303.71, 72.78) * mm});
            skLineSegment(sketch, "E62", {"start": v(-303.71, 72.78) * mm, "end": v(-151.14, 72.78) * mm});
            skLineSegment(sketch, "E63", {"start": v(-151.14, 72.78) * mm, "end": v(-26.69, 35) * mm});
            skLineSegment(sketch, "E64", {"start": v(-432.69, -35) * mm, "end": v(-388.9, -53.91) * mm});
            skLineSegment(sketch, "E65", {"start": v(-388.9, -53.91) * mm, "end": v(-192.66, -53.91) * mm});
            skLineSegment(sketch, "E66", {"start": v(-192.66, -53.91) * mm, "end": v(-26.69, -35) * mm});
            skSolve(sketch);
        }
        {
            var Q0;
            {var subQ16=sQuery(id+"F20.wireOp",EDGE,"E60.0");Q0=makeQuery(id+"F20.imprint","IMPRINT",FACE,{"disambiguationData":[TD([[makeQuery(id+"F20.imprint","IMPRINT",EDGE,{"derivedFrom":subQ16}),1.0]])]});}
            var Q1;
            Q1=makeQuery(id+"F20.imprint","IMPRINT",FACE,{"disambiguationData":[TD([[makeQuery(id+"F20.imprint","IMPRINT",EDGE,{"derivedFrom":sQuery(id+"F20.wireOp",EDGE,"E61")}),-1.0]])]});
            var Q2;
            {var subQ0=sQuery(id+"F20.wireOp",EDGE,"E59.0");Q2=makeQuery(id+"F20.imprint","IMPRINT",FACE,{"disambiguationData":[TD([[makeQuery(id+"F20.imprint","IMPRINT",EDGE,{"derivedFrom":subQ0}),-1.0]])]});}
            var Q3;
            Q3=makeQuery(id+"F20.imprint","IMPRINT",FACE,{"disambiguationData":[TD([[makeQuery(id+"F20.imprint","IMPRINT",EDGE,{"derivedFrom":sQuery(id+"F20.wireOp",EDGE,"E64")}),1.0]])]});
            extrude(context, id + "F21", {"entities" : qUnion([Q0, Q1, Q2, Q3]), "operationType" : NewBodyOperationType.REMOVE, "oppositeDirection" : true, "depth" : 25 * mm, "offsetDistance" : 25 * mm});
        }
        {
            var Q0;
            {var subQ0=makeQuery(id+"F3.opExtrude","CAP_FACE",FACE,{"disambiguationData":[OSD([sQuery(id+"F2.wireOp",EDGE,"E16.0"),sQuery(id+"F2.wireOp",EDGE,"E16.1"),sQuery(id+"F2.wireOp",EDGE,"E16.2"),sQuery(id+"F2.wireOp",EDGE,"E16.3"),sQuery(id+"F2.wireOp",EDGE,"E16.4"),sQuery(id+"F2.wireOp",EDGE,"E16.5"),sQuery(id+"F2.wireOp",EDGE,"E16.6"),sQuery(id+"F2.wireOp",EDGE,"E16.7"),sQuery(id+"F2.wireOp",EDGE,"E18.0"),sQuery(id+"F2.wireOp",EDGE,"E19.0"),sQuery(id+"F2.wireOp",EDGE,"E20"),sQuery(id+"F2.wireOp",EDGE,"E21.trimOffspring"),sQuery(id+"F2.wireOp",EDGE,"E22.0"),sQuery(id+"F2.wireOp",EDGE,"E23.0"),sQuery(id+"F2.wireOp",EDGE,"E24.0"),sQuery(id+"F2.wireOp",EDGE,"E25.0"),sQuery(id+"F2.wireOp",EDGE,"E26.0"),sQuery(id+"F2.wireOp",EDGE,"E27.0"),sQuery(id+"F2.wireOp",EDGE,"E28.0"),sQuery(id+"F2.wireOp",EDGE,"E29.0")])],"isStart":false});Q0=makeQuery(id+"F7.boolean.opBoolean","MERGE",FACE,{"derivedFrom":[makeQuery(id+"F5.boolean.opBoolean","MERGE",FACE,{"derivedFrom":[subQ0,makeQuery(id+"F5.opPattern","COPY",FACE,{"derivedFrom":subQ0,"instanceName":"1"})]}),makeQuery(id+"F7.opExtrude","CAP_FACE",FACE,{"disambiguationData":[OSD([sQuery(id+"F6.wireOp",EDGE,"E30"),sQuery(id+"F6.wireOp",EDGE,"E31"),sQuery(id+"F6.wireOp",EDGE,"E32"),sQuery(id+"F6.wireOp",EDGE,"E33"),sQuery(id+"F6.wireOp",EDGE,"E34")])],"isStart":true})]});}
            var sketch = newSketch(context, id + "F22", { "sketchPlane" : qUnion([Q0])});
            skLineSegment(sketch, "E67", {"start": v(-486.19, 0) * mm, "end": v(-566.19, 0) * mm, "construction": true});
            skLineSegment(sketch, "E68.bottom", {"start": v(-616.19, -52.5) * mm, "end": v(-516.19, -52.5) * mm});
            skLineSegment(sketch, "E68.top", {"start": v(-616.19, 52.5) * mm, "end": v(-516.19, 52.5) * mm});
            skLineSegment(sketch, "E68.left", {"start": v(-616.19, -52.5) * mm, "end": v(-616.19, 52.5) * mm});
            skLineSegment(sketch, "E68.right", {"start": v(-516.19, -52.5) * mm, "end": v(-516.19, 52.5) * mm});
            skPoint(sketch, "E68.middle", {"position": v(-566.19, 0) * mm});
            skLineSegment(sketch, "E69.0", {"start": v(-626.19, 62.5) * mm, "end": v(-506.19, 62.5) * mm});
            skLineSegment(sketch, "E69.1", {"start": v(-626.19, -62.5) * mm, "end": v(-626.19, 62.5) * mm});
            skLineSegment(sketch, "E69.2", {"start": v(-626.19, -62.5) * mm, "end": v(-506.19, -62.5) * mm});
            skLineSegment(sketch, "E69.3", {"start": v(-506.19, -62.5) * mm, "end": v(-506.19, 62.5) * mm});
            skLineSegment(sketch, "E70", {"start": v(-486.19, 25) * mm, "end": v(-506.19, 25) * mm});
            skLineSegment(sketch, "E71.MirrorCS", {"start": v(-486.19, -25) * mm, "end": v(-506.19, -25) * mm});
            skSolve(sketch);
        }
        {
            var Q0;
            {var subQ0=sQuery(id+"F22.wireOp",EDGE,"E70");Q0=makeQuery(id+"F22.imprint","IMPRINT",FACE,{"disambiguationData":[TD([[makeQuery(id+"F22.imprint","IMPRINT",EDGE,{"derivedFrom":subQ0}),1.0]])]});}
            var Q1;
            Q1=makeQuery(id+"F22.imprint","IMPRINT",FACE,{"disambiguationData":[TD([[makeQuery(id+"F22.imprint","IMPRINT",EDGE,{"derivedFrom":sQuery(id+"F22.wireOp",EDGE,"E68.bottom")}),-1.0]])]});
            var Q2;
            {var subQ0=makeQuery(id+"F3.boolean.opBoolean","MERGE",FACE,{"derivedFrom":[makeQuery(id+"F1.opExtrude","CAP_FACE",FACE,{"disambiguationData":[OSD([sQuery(id+"F0.wireOp",EDGE,"E0.0"),sQuery(id+"F0.wireOp",EDGE,"E1.0"),sQuery(id+"F0.wireOp",EDGE,"E4.0"),sQuery(id+"F0.wireOp",EDGE,"E5.0"),sQuery(id+"F0.wireOp",EDGE,"E6.0"),sQuery(id+"F0.wireOp",EDGE,"E7.0"),sQuery(id+"F0.wireOp",EDGE,"E8.0"),sQuery(id+"F0.wireOp",EDGE,"E9.0"),sQuery(id+"F0.wireOp",EDGE,"E10.0"),sQuery(id+"F0.wireOp",EDGE,"E12.0"),sQuery(id+"F0.wireOp",EDGE,"E13.0"),sQuery(id+"F0.wireOp",EDGE,"E15.0")])],"isStart":true}),makeQuery(id+"F3.opExtrude","CAP_FACE",FACE,{"disambiguationData":[OSD([sQuery(id+"F2.wireOp",EDGE,"E16.0"),sQuery(id+"F2.wireOp",EDGE,"E16.1"),sQuery(id+"F2.wireOp",EDGE,"E16.2"),sQuery(id+"F2.wireOp",EDGE,"E16.3"),sQuery(id+"F2.wireOp",EDGE,"E16.4"),sQuery(id+"F2.wireOp",EDGE,"E16.5"),sQuery(id+"F2.wireOp",EDGE,"E16.6"),sQuery(id+"F2.wireOp",EDGE,"E16.7"),sQuery(id+"F2.wireOp",EDGE,"E18.0"),sQuery(id+"F2.wireOp",EDGE,"E19.0"),sQuery(id+"F2.wireOp",EDGE,"E20"),sQuery(id+"F2.wireOp",EDGE,"E21.trimOffspring"),sQuery(id+"F2.wireOp",EDGE,"E22.0"),sQuery(id+"F2.wireOp",EDGE,"E23.0"),sQuery(id+"F2.wireOp",EDGE,"E24.0"),sQuery(id+"F2.wireOp",EDGE,"E25.0"),sQuery(id+"F2.wireOp",EDGE,"E26.0"),sQuery(id+"F2.wireOp",EDGE,"E27.0"),sQuery(id+"F2.wireOp",EDGE,"E28.0"),sQuery(id+"F2.wireOp",EDGE,"E29.0")])],"isStart":true})]});Q2=makeQuery(id+"F7.boolean.opBoolean","MERGE",FACE,{"derivedFrom":[makeQuery(id+"F5.boolean.opBoolean","MERGE",FACE,{"derivedFrom":[subQ0,makeQuery(id+"F5.opPattern","COPY",FACE,{"derivedFrom":subQ0,"instanceName":"1"})]}),makeQuery(id+"F7.opExtrude","CAP_FACE",FACE,{"disambiguationData":[OSD([sQuery(id+"F6.wireOp",EDGE,"E30"),sQuery(id+"F6.wireOp",EDGE,"E31"),sQuery(id+"F6.wireOp",EDGE,"E32"),sQuery(id+"F6.wireOp",EDGE,"E33"),sQuery(id+"F6.wireOp",EDGE,"E34")])],"isStart":false})]});}
            extrude(context, id + "F23", {"entities" : qUnion([Q0, Q1]), "operationType" : NewBodyOperationType.ADD, "endBound" : BoundingType.UP_TO_SURFACE, "oppositeDirection" : true, "depth" : 25 * mm, "endBoundEntityFace" : qUnion([Q2]), "offsetDistance" : 25 * mm});
        }
        {
            var Q0;
            Q0=makeQuery(id+"F23.opExtrude","SWEPT_EDGE",EDGE,{"disambiguationData":[OSD([sQuery(id+"F22.wireOp",EDGE,"E69.0"),sQuery(id+"F22.wireOp",EDGE,"E69.1")])]});
            var Q1;
            Q1=makeQuery(id+"F23.opExtrude","SWEPT_EDGE",EDGE,{"disambiguationData":[OSD([sQuery(id+"F22.wireOp",EDGE,"E69.0"),sQuery(id+"F22.wireOp",EDGE,"E69.3")])]});
            var Q2;
            Q2=makeQuery(id+"F23.opExtrude","SWEPT_EDGE",EDGE,{"disambiguationData":[OSD([sQuery(id+"F2.wireOp",EDGE,"E16.7"),sQuery(id+"F22.wireOp",EDGE,"E70")])]});
            var Q3;
            Q3=makeQuery(id+"F23.opExtrude","SWEPT_EDGE",EDGE,{"disambiguationData":[OSD([sQuery(id+"F22.wireOp",EDGE,"E69.3"),sQuery(id+"F22.wireOp",EDGE,"E70")])]});
            var Q4;
            Q4=makeQuery(id+"F23.opExtrude","SWEPT_EDGE",EDGE,{"disambiguationData":[OSD([sQuery(id+"F2.wireOp",EDGE,"E16.7"),sQuery(id+"F22.wireOp",EDGE,"E71.MirrorCS")])]});
            var Q5;
            Q5=makeQuery(id+"F23.opExtrude","SWEPT_EDGE",EDGE,{"disambiguationData":[OSD([sQuery(id+"F22.wireOp",EDGE,"E69.3"),sQuery(id+"F22.wireOp",EDGE,"E71.MirrorCS")])]});
            var Q6;
            Q6=makeQuery(id+"F23.opExtrude","SWEPT_EDGE",EDGE,{"disambiguationData":[OSD([sQuery(id+"F22.wireOp",EDGE,"E69.2"),sQuery(id+"F22.wireOp",EDGE,"E69.3")])]});
            var Q7;
            Q7=makeQuery(id+"F23.opExtrude","SWEPT_EDGE",EDGE,{"disambiguationData":[OSD([sQuery(id+"F22.wireOp",EDGE,"E69.1"),sQuery(id+"F22.wireOp",EDGE,"E69.2")])]});
            fillet(context, id + "F24", {"entities" : qUnion([Q0, Q1, Q2, Q3, Q4, Q5, Q6, Q7]), "radius" : 5 * mm, "tangentPropagation" : true, "allowEdgeOverflow" : false});
        }
    });
